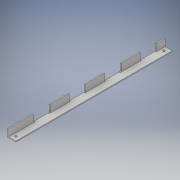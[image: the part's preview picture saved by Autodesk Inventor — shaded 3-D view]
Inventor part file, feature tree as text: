
AUTODESK INVENTOR PART (.ipt)
format: ipt  version: 2017 (Build 210142000, 142)  size: 154,624 bytes
history: native  units: in
note: dims shown in document units (in); Inventor stores cm internally (conversion verified against a paired STEP export)
features: extrude x2, sketch x2, hole x1, pattern_linear x1
ambient origin geometry x8: Origin, YZ Plane, XZ Plane, XY Plane, X Axis, Y Axis, Z Axis, Center Point
bodies: Solid1 (feature_tree)
feature tree (6):
  extrude  "Extrusion1"  Depth=1.0in
  hole  "Hole1"  [1 undecoded]
  extrude  "Extrusion11"  Depth=4.4in
  pattern_linear  "Rectangular Pattern1"  Spacing1=0.5in  [1 undecoded]
  sketch  "Sketch2"  dims[d0=1.0in d1=1.0in]
  sketch  "Sketch22"  dims[d2=0.125in d3=19.375in d4=0.0in d5=0.5in d6=0.5in d7=0.7874in d9=18.375in d10=0.3937in d12=1.0in d14=0.266in d15=0.75in d16=0.385in d17=0.25in d18=0.5635in d19=1.0in d20=0.8108in d31=0.5in d137=2.0625in d138=3.0625in d139=0.125in d140=1.0in d141=0.0in d144=1.5748in d146=4.4in]
note: 2 required parameter values undecoded (feature->parameter linkage not recoverable at this tier; creation-order binding heuristic only, values carry confidence <= 0.55)
